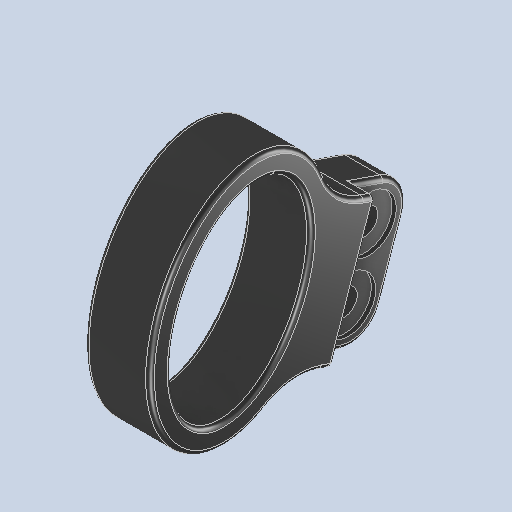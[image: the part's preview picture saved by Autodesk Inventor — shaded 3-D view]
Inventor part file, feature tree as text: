
AUTODESK INVENTOR PART (.ipt)
format: ipt  version: 2024.2 (Build 282272000, 272)  size: 386,560 bytes
history: native  units: mm
features: fillet x3, extrude x2, other x1, sketch x1, hole x1
ambient origin geometry x8: Origin, YZ Plane, XZ Plane, XY Plane, X Axis, Y Axis, Z Axis, Center Point
bodies: Body1 (feature_tree)
feature tree (8):
  other  "TorsoSideFrame.ipt"
  sketch  "Sketch5"  dims[d56=10.0mm d57=10.0mm d58=0.0mm d59=6.0mm d60=6.0mm d61=12.5mm d62=1.0mm d63=90.0deg d64=2.5mm d65=0.0mm d75=15.0mm d76=1.0mm d77=7.5mm d83=5.0mm d84=0.0mm d40=0.0mm d41=0.0mm d42=0.0mm d43=0.0mm d79=0.5mm d80=0.872665mm d81=0.5mm d82=0.872665mm]
  extrude  "Extrusion2"  Depth=10.0mm TaperAngle=0.0deg
  extrude  "Extrusion5"  Depth=15.0mm
  hole  "Hole3"  [1 undecoded]
  fillet  "Fillet9"  Radius=7.5mm
  fillet  "Fillet10"  Radius=5.0mm
  fillet  "Fillet11"  [1 undecoded]
note: 2 required parameter values undecoded (feature->parameter linkage not recoverable at this tier; creation-order binding heuristic only, values carry confidence <= 0.55)
